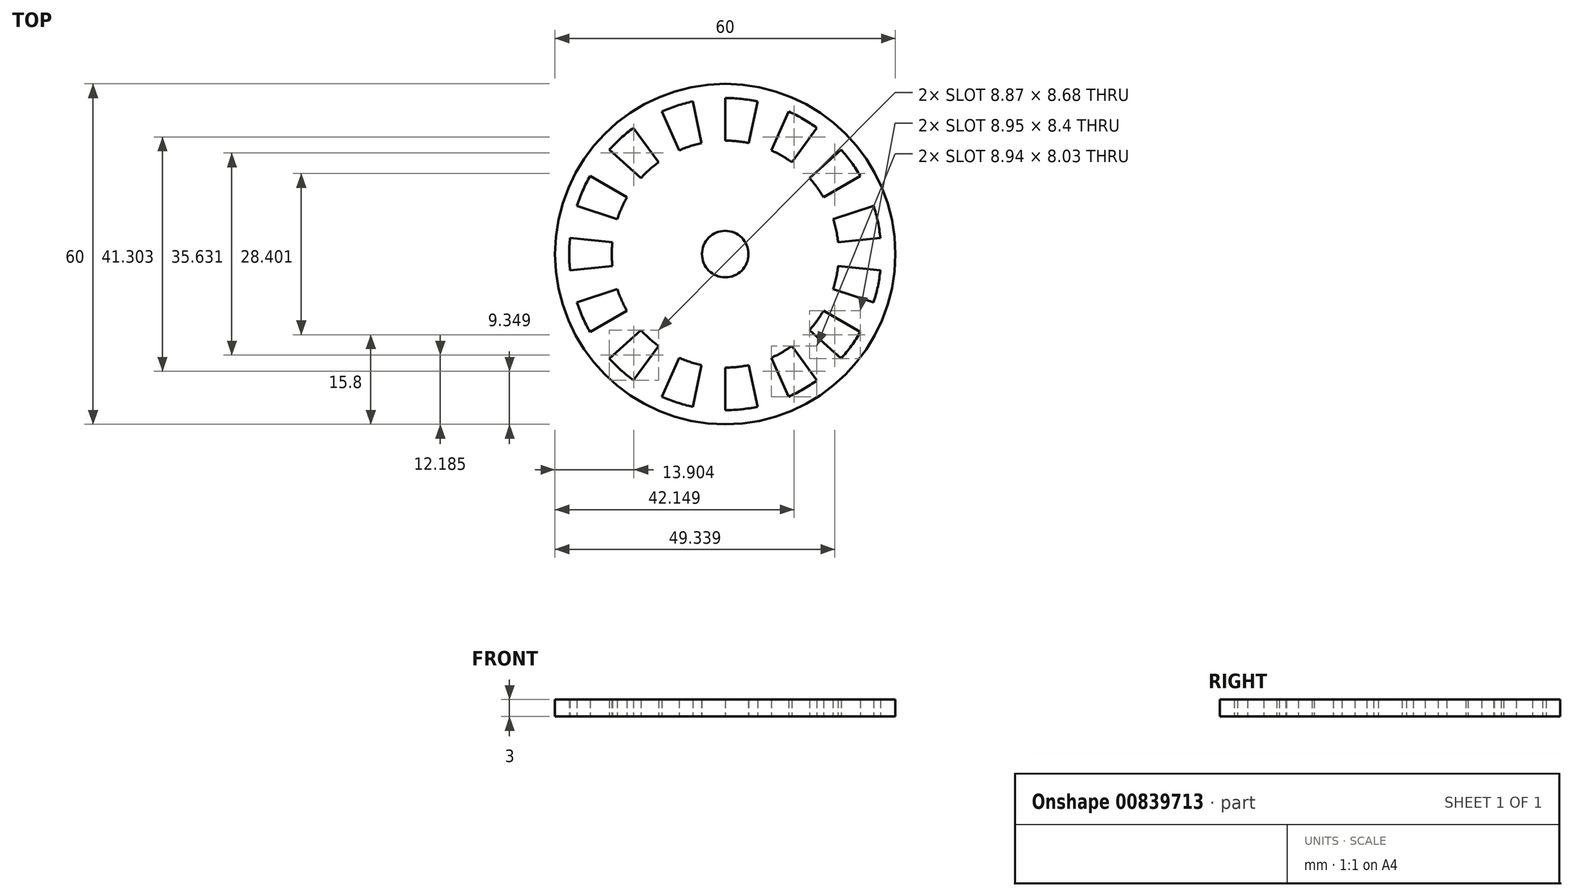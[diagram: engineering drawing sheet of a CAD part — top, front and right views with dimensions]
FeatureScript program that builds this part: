
annotation { "Feature Type Name" : "Feature", "Feature Type Description" : "" }
export const myFeature = defineFeature(function(context is Context, id is Id, definition is map)
    precondition{}
    {
        {
            var Q0;
            Q0=qCreatedBy(makeId("Top.planeOp"),FACE);
            var sketch = newSketch(context, id + "F0", { "sketchPlane" : qUnion([Q0])});
            skCircle(sketch, "E0", {"center": v(0, 0) * mm, "radius": 30 * mm});
            skArc(sketch, "E1", {"start": v(-5.72, 26.9) * mm, "mid": v(-8.5, 26.15) * mm, "end": v(-11.19, 25.12) * mm});
            skArc(sketch, "E2", {"start": v(-4.16, 19.56) * mm, "mid": v(-6.18, 19.02) * mm, "end": v(-8.13, 18.27) * mm});
            skCircle(sketch, "E3", {"center": v(0, 0) * mm, "radius": 4.1 * mm});
            skLineSegment(sketch, "E4", {"start": v(0, 27.5) * mm, "end": v(0, 20) * mm});
            skLineSegment(sketch, "E5.1.0", {"start": v(-5.72, 26.9) * mm, "end": v(-4.16, 19.56) * mm});
            skLineSegment(sketch, "E5.2.0", {"start": v(-11.19, 25.12) * mm, "end": v(-8.13, 18.27) * mm});
            skLineSegment(sketch, "E6.2.3.0", {"start": v(-16.16, 22.25) * mm, "end": v(-11.76, 16.18) * mm});
            skLineSegment(sketch, "E6.2.4.0", {"start": v(-20.44, 18.4) * mm, "end": v(-14.86, 13.38) * mm});
            skLineSegment(sketch, "E6.2.5.0", {"start": v(-23.82, 13.75) * mm, "end": v(-17.32, 10) * mm});
            skLineSegment(sketch, "E6.2.6.0", {"start": v(-26.15, 8.5) * mm, "end": v(-19.02, 6.18) * mm});
            skLineSegment(sketch, "E6.2.7.0", {"start": v(-27.35, 2.87) * mm, "end": v(-19.9, 2.1) * mm});
            skLineSegment(sketch, "E6.2.8.0", {"start": v(-27.35, -2.87) * mm, "end": v(-19.9, -2.1) * mm});
            skLineSegment(sketch, "E6.2.9.0", {"start": v(-26.15, -8.5) * mm, "end": v(-19.02, -6.18) * mm});
            skLineSegment(sketch, "E6.2.10.0", {"start": v(-23.82, -13.75) * mm, "end": v(-17.32, -10) * mm});
            skLineSegment(sketch, "E6.2.11.0", {"start": v(-20.44, -18.4) * mm, "end": v(-14.86, -13.38) * mm});
            skLineSegment(sketch, "E6.2.12.0", {"start": v(-16.16, -22.25) * mm, "end": v(-11.76, -16.18) * mm});
            skLineSegment(sketch, "E6.2.13.0", {"start": v(-11.19, -25.12) * mm, "end": v(-8.13, -18.27) * mm});
            skLineSegment(sketch, "E6.2.14.0", {"start": v(-5.72, -26.9) * mm, "end": v(-4.16, -19.56) * mm});
            skLineSegment(sketch, "E6.2.15.0", {"start": v(0, -27.5) * mm, "end": v(0, -20) * mm});
            skLineSegment(sketch, "E6.2.16.0", {"start": v(5.72, -26.9) * mm, "end": v(4.16, -19.56) * mm});
            skLineSegment(sketch, "E6.2.17.0", {"start": v(11.19, -25.12) * mm, "end": v(8.13, -18.27) * mm});
            skLineSegment(sketch, "E6.2.18.0", {"start": v(16.16, -22.25) * mm, "end": v(11.76, -16.18) * mm});
            skLineSegment(sketch, "E6.2.19.0", {"start": v(20.44, -18.4) * mm, "end": v(14.86, -13.38) * mm});
            skLineSegment(sketch, "E6.2.20.0", {"start": v(23.82, -13.75) * mm, "end": v(17.32, -10) * mm});
            skLineSegment(sketch, "E6.2.21.0", {"start": v(26.15, -8.5) * mm, "end": v(19.02, -6.18) * mm});
            skLineSegment(sketch, "E6.2.22.0", {"start": v(27.35, -2.87) * mm, "end": v(19.9, -2.1) * mm});
            skLineSegment(sketch, "E6.2.23.0", {"start": v(27.35, 2.87) * mm, "end": v(19.9, 2.1) * mm});
            skLineSegment(sketch, "E6.2.24.0", {"start": v(26.15, 8.5) * mm, "end": v(19.02, 6.18) * mm});
            skLineSegment(sketch, "E6.2.25.0", {"start": v(23.82, 13.75) * mm, "end": v(17.32, 10) * mm});
            skLineSegment(sketch, "E6.2.26.0", {"start": v(20.44, 18.4) * mm, "end": v(14.86, 13.38) * mm});
            skLineSegment(sketch, "E6.2.27.0", {"start": v(16.16, 22.25) * mm, "end": v(11.76, 16.18) * mm});
            skLineSegment(sketch, "E6.2.28.0", {"start": v(11.19, 25.12) * mm, "end": v(8.13, 18.27) * mm});
            skLineSegment(sketch, "E6.2.29.0", {"start": v(5.72, 26.9) * mm, "end": v(4.16, 19.56) * mm});
            skArc(sketch, "E7.trimOffspring", {"start": v(-11.76, 16.18) * mm, "mid": v(-13.38, 14.86) * mm, "end": v(-14.86, 13.38) * mm});
            skArc(sketch, "E8.trimOffspring", {"start": v(-16.16, 22.25) * mm, "mid": v(-18.4, 20.44) * mm, "end": v(-20.44, 18.4) * mm});
            skArc(sketch, "E9.trimOffspring", {"start": v(-23.82, 13.75) * mm, "mid": v(-25.12, 11.19) * mm, "end": v(-26.15, 8.5) * mm});
            skArc(sketch, "E10.trimOffspring", {"start": v(-17.32, 10) * mm, "mid": v(-18.27, 8.13) * mm, "end": v(-19.02, 6.18) * mm});
            skArc(sketch, "E11.trimOffspring", {"start": v(-27.35, 2.87) * mm, "mid": v(-27.5, 0) * mm, "end": v(-27.35, -2.87) * mm});
            skArc(sketch, "E12.trimOffspring", {"start": v(-19.9, 2.1) * mm, "mid": v(-20, 0) * mm, "end": v(-19.9, -2.1) * mm});
            skArc(sketch, "E13.trimOffspring", {"start": v(-26.15, -8.5) * mm, "mid": v(-25.12, -11.19) * mm, "end": v(-23.82, -13.75) * mm});
            skArc(sketch, "E14.trimOffspring", {"start": v(-19.02, -6.18) * mm, "mid": v(-18.27, -8.13) * mm, "end": v(-17.32, -10) * mm});
            skArc(sketch, "E15.trimOffspring", {"start": v(-20.44, -18.4) * mm, "mid": v(-18.4, -20.44) * mm, "end": v(-16.16, -22.25) * mm});
            skArc(sketch, "E16.trimOffspring", {"start": v(-14.86, -13.38) * mm, "mid": v(-13.38, -14.86) * mm, "end": v(-11.76, -16.18) * mm});
            skArc(sketch, "E17.trimOffspring", {"start": v(-11.19, -25.12) * mm, "mid": v(-8.5, -26.15) * mm, "end": v(-5.72, -26.9) * mm});
            skArc(sketch, "E18.trimOffspring", {"start": v(-8.13, -18.27) * mm, "mid": v(-6.18, -19.02) * mm, "end": v(-4.16, -19.56) * mm});
            skArc(sketch, "E19.trimOffspring", {"start": v(0, -27.5) * mm, "mid": v(2.87, -27.35) * mm, "end": v(5.72, -26.9) * mm});
            skArc(sketch, "E20.trimOffspring", {"start": v(0, -20) * mm, "mid": v(2.1, -19.9) * mm, "end": v(4.16, -19.56) * mm});
            skArc(sketch, "E21.trimOffspring", {"start": v(8.13, -18.27) * mm, "mid": v(10, -17.32) * mm, "end": v(11.76, -16.18) * mm});
            skArc(sketch, "E22.trimOffspring", {"start": v(11.19, -25.12) * mm, "mid": v(13.75, -23.82) * mm, "end": v(16.16, -22.25) * mm});
            skArc(sketch, "E23.trimOffspring", {"start": v(20.44, -18.4) * mm, "mid": v(22.25, -16.16) * mm, "end": v(23.82, -13.75) * mm});
            skArc(sketch, "E24.trimOffspring", {"start": v(14.86, -13.38) * mm, "mid": v(16.18, -11.76) * mm, "end": v(17.32, -10) * mm});
            skArc(sketch, "E25.trimOffspring", {"start": v(19.02, -6.18) * mm, "mid": v(19.56, -4.16) * mm, "end": v(19.9, -2.1) * mm});
            skArc(sketch, "E26.trimOffspring", {"start": v(26.15, -8.5) * mm, "mid": v(26.9, -5.72) * mm, "end": v(27.35, -2.87) * mm});
            skArc(sketch, "E27.trimOffspring", {"start": v(19.9, 2.1) * mm, "mid": v(19.56, 4.16) * mm, "end": v(19.02, 6.18) * mm});
            skArc(sketch, "E28.trimOffspring", {"start": v(27.35, 2.87) * mm, "mid": v(26.9, 5.72) * mm, "end": v(26.15, 8.5) * mm});
            skArc(sketch, "E29.trimOffspring", {"start": v(17.32, 10) * mm, "mid": v(16.18, 11.76) * mm, "end": v(14.86, 13.38) * mm});
            skArc(sketch, "E30.trimOffspring", {"start": v(23.82, 13.75) * mm, "mid": v(22.25, 16.16) * mm, "end": v(20.44, 18.4) * mm});
            skArc(sketch, "E31.trimOffspring", {"start": v(11.76, 16.18) * mm, "mid": v(10, 17.32) * mm, "end": v(8.13, 18.27) * mm});
            skArc(sketch, "E32.trimOffspring", {"start": v(16.16, 22.25) * mm, "mid": v(13.75, 23.82) * mm, "end": v(11.19, 25.12) * mm});
            skArc(sketch, "E33.trimOffspring", {"start": v(5.72, 26.9) * mm, "mid": v(2.87, 27.35) * mm, "end": v(0, 27.5) * mm});
            skArc(sketch, "E34.trimOffspring", {"start": v(4.16, 19.56) * mm, "mid": v(2.1, 19.9) * mm, "end": v(0, 20) * mm});
            skSolve(sketch);
        }
        {
            var Q0;
            Q0=makeQuery(id+"F0.imprint","IMPRINT",FACE,{"disambiguationData":[TD([[makeQuery(id+"F0.imprint","IMPRINT",EDGE,{"derivedFrom":sQuery(id+"F0.wireOp",EDGE,"E0")}),1.0]])]});
            extrude(context, id + "F1", {"entities" : qUnion([Q0]), "depth" : 3 * mm, "offsetDistance" : 25 * mm});
        }
    });
